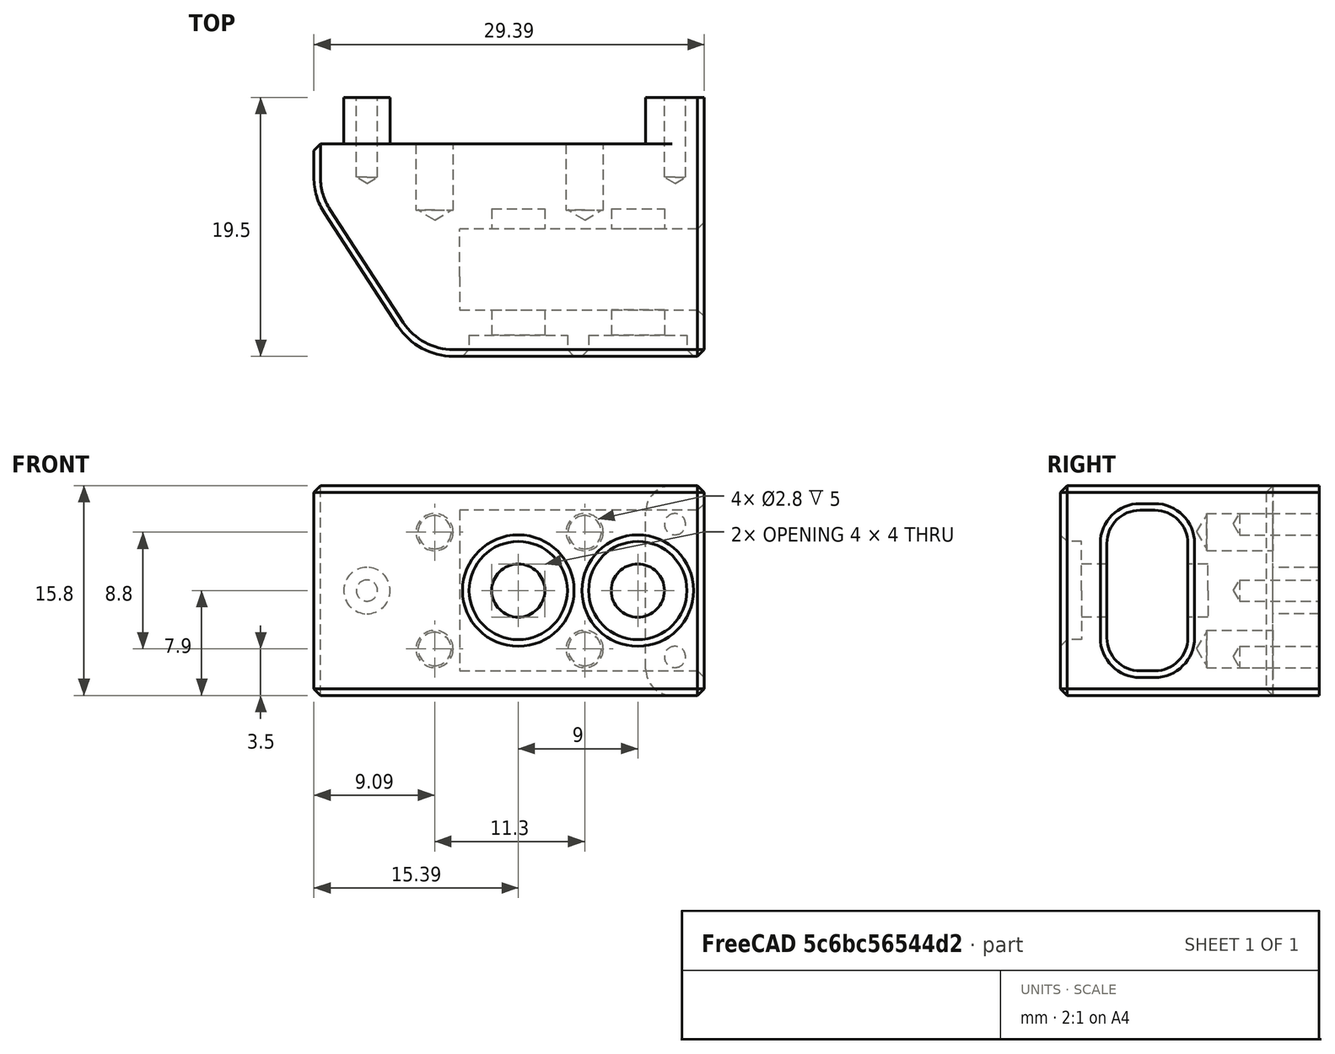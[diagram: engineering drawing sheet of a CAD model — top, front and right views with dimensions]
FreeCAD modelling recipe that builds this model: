
FCSTD DOCUMENT  (FreeCAD 0.18R16146 (Git))
Label: ResizedEndEffector
License: All rights reserved
LicenseURL: http://en.wikipedia.org/wiki/All_rights_reserved
objects: Part::Feature×1, PartDesign::FeatureBase×1, Sketcher::SketchObject×1, PartDesign::Pocket×1, PartDesign::Body×1
note: 6 computed .brp shape members not serialized (recipe doc carries the construction recipe); baked Part::Feature solids carry a one-line shape summary decoded from their .brp

FEATURE [Part::Feature] Part__Feature091  label="EndEffector"
  Placement = pos=(-59.5544,190.649,-119.954) rot=(0.000298,1,0;3.14159rad)
  shape: bbox 29.4 x 19.51 x 15.8 mm, 97 faces (baked)
FEATURE [PartDesign::FeatureBase] BaseFeature
  BaseFeature = -> Part__Feature091
FEATURE [Sketcher::SketchObject] Sketch
  ExternalGeometry = -> [BaseFeature]
  MapMode = 5
  Placement = pos=(0,16,0) rot=(0,0.707107,0.707107;3.14159rad)
  Support = -> [BaseFeature]
  sketch-geometry (4):
    g0: Circle CenterX=-12.6 CenterY=4.4 CenterZ=0 NormalX=0 NormalY=0 NormalZ=1 AngleXU=0 Radius=1.4
    g1: Circle CenterX=-1.3 CenterY=4.4 CenterZ=0 NormalX=0 NormalY=0 NormalZ=1 AngleXU=0 Radius=1.4
    g2: Circle CenterX=-12.6 CenterY=-4.4 CenterZ=0 NormalX=0 NormalY=0 NormalZ=1 AngleXU=0 Radius=1.4
    g3: Circle CenterX=-1.3 CenterY=-4.4 CenterZ=0 NormalX=0 NormalY=0 NormalZ=1 AngleXU=0 Radius=1.4
  constraints (8):
    c: Coincident(g0,g-4)
    c: Radius(g0) = 1.4
    c: Coincident(g1,g-10)
    c: Radius(g1) = 1.4
    c: Coincident(g2,g-6)
    c: Radius(g2) = 1.4
    c: Coincident(g3,g-8)
    c: Radius(g3) = 1.4
FEATURE [PartDesign::Pocket] Pocket
  BaseFeature = -> BaseFeature
  Length = 5
  Length2 = 100
  Profile = -> Sketch
  Type = 0
FEATURE [PartDesign::Body] Body
  BaseFeature = -> Part__Feature091
  Group = -> [BaseFeature,Sketch,Pocket]
  Origin = -> Origin
  Tip = -> Pocket
